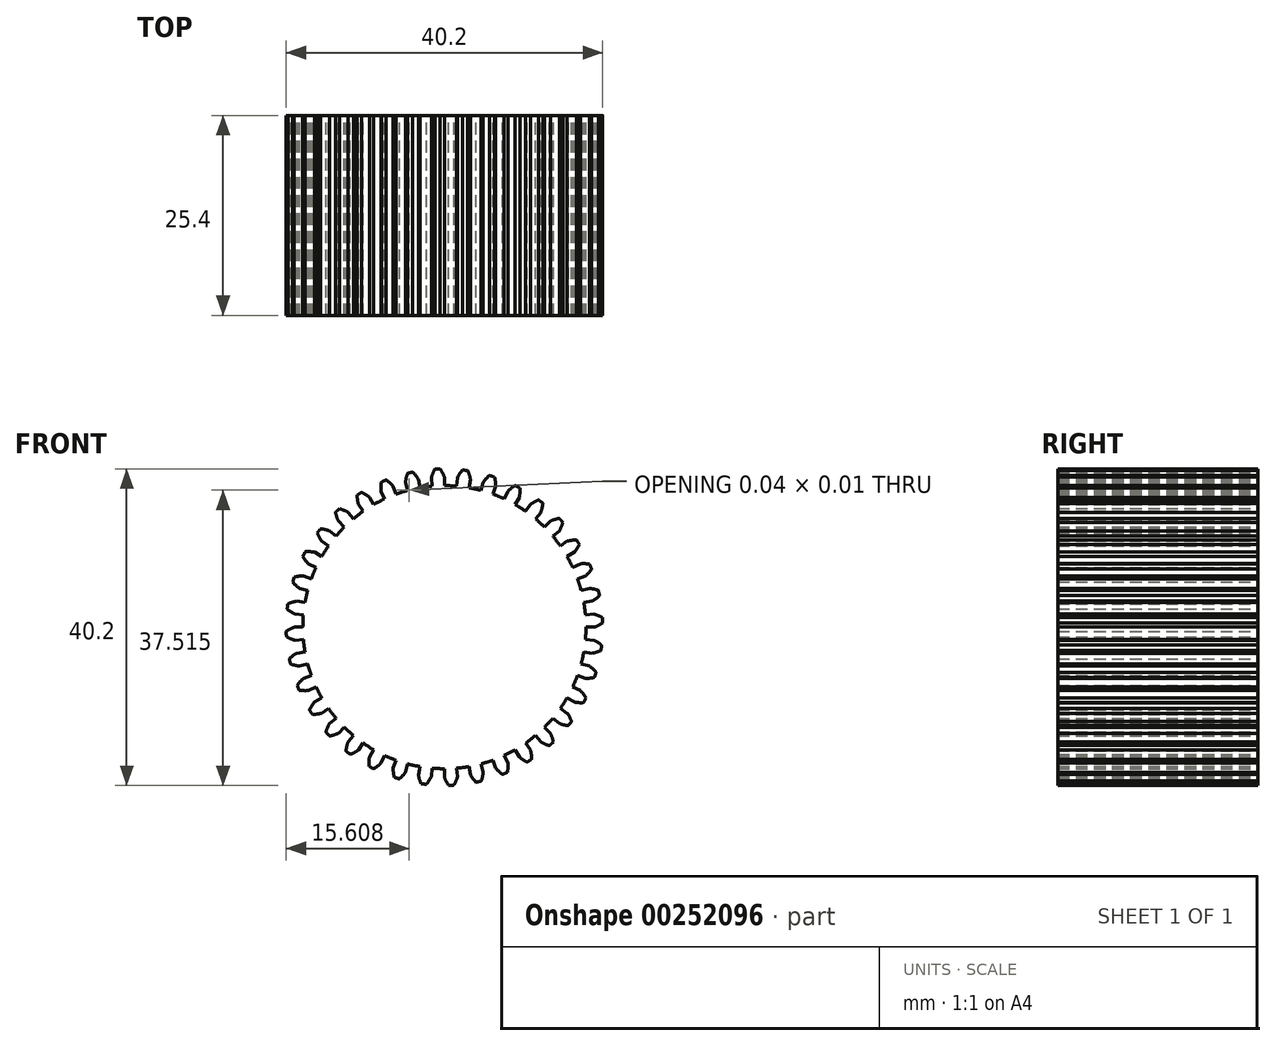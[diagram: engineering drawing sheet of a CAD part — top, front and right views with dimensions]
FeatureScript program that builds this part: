
annotation { "Feature Type Name" : "Feature", "Feature Type Description" : "" }
export const myFeature = defineFeature(function(context is Context, id is Id, definition is map)
    precondition{}
    {
        {
            var Q0;
            Q0=qCreatedBy(makeId("Front.planeOp"),FACE);
            var sketch = newSketch(context, id + "F0", { "sketchPlane" : qUnion([Q0])});
            skArc(sketch, "E0", {"start": v(-0.54, 20.1) * mm, "mid": v(-0.7, 20.1) * mm, "end": v(-0.88, 20.08) * mm});
            skArc(sketch, "E1", {"start": v(1.57, 17.91) * mm, "mid": v(0.7, 17.97) * mm, "end": v(-0.19, 17.98) * mm});
            skLineSegment(sketch, "E2", {"start": v(0, 17.98) * mm, "end": v(0, 19.05) * mm});
            skLineSegment(sketch, "E3", {"start": v(-4.48, 17.42) * mm, "end": v(-4.51, 17.4) * mm});
            skLineSegment(sketch, "E4", {"start": v(0, 0) * mm, "end": v(-0.88, 20.08) * mm});
            skArc(sketch, "E5", {"start": v(4.45, 17.34) * mm, "mid": v(4.46, 17.38) * mm, "end": v(4.47, 17.42) * mm});
            skArc(sketch, "E6.trimOffspring", {"start": v(0, 19.05) * mm, "mid": v(-0.24, 19.6) * mm, "end": v(-0.54, 20.1) * mm});
            skArc(sketch, "E7.trimOffspring", {"start": v(-4.48, 17.42) * mm, "mid": v(-4.46, 17.38) * mm, "end": v(-4.45, 17.34) * mm});
            skLineSegment(sketch, "E8.trimOffspring", {"start": v(-1.66, 18.98) * mm, "end": v(-1.67, 19.05) * mm});
            skArc(sketch, "E9.trimOffspring", {"start": v(-8.95, 15.8) * mm, "mid": v(-8.9, 15.67) * mm, "end": v(-8.86, 15.56) * mm});
            skLineSegment(sketch, "E10.MirrorCS", {"start": v(-1.57, 17.91) * mm, "end": v(-1.66, 18.98) * mm});
            skArc(sketch, "E11.MirrorCS", {"start": v(-1.66, 18.98) * mm, "mid": v(-1.47, 19.54) * mm, "end": v(-1.22, 20.07) * mm});
            skArc(sketch, "E12.MirrorCS", {"start": v(-1.22, 20.07) * mm, "mid": v(-1.05, 20.08) * mm, "end": v(-0.88, 20.08) * mm});
            skLineSegment(sketch, "E13.1.0", {"start": v(-4.65, 17.37) * mm, "end": v(-4.93, 18.4) * mm});
            skArc(sketch, "E13.1.1", {"start": v(-4.93, 18.4) * mm, "mid": v(-4.84, 18.98) * mm, "end": v(-4.68, 19.55) * mm});
            skArc(sketch, "E13.1.2", {"start": v(-4.68, 19.55) * mm, "mid": v(-4.52, 19.59) * mm, "end": v(-4.35, 19.63) * mm});
            skArc(sketch, "E13.1.3", {"start": v(-4.02, 19.7) * mm, "mid": v(-4.18, 19.66) * mm, "end": v(-4.35, 19.63) * mm});
            skArc(sketch, "E13.1.4", {"start": v(-3.3, 18.76) * mm, "mid": v(-3.63, 19.25) * mm, "end": v(-4.02, 19.7) * mm});
            skLineSegment(sketch, "E13.1.5", {"start": v(-3.12, 17.7) * mm, "end": v(-3.3, 18.76) * mm});
            skLineSegment(sketch, "E13.2.0", {"start": v(-7.6, 16.3) * mm, "end": v(-8.05, 17.27) * mm});
            skArc(sketch, "E13.2.1", {"start": v(-8.05, 17.27) * mm, "mid": v(-8.07, 17.85) * mm, "end": v(-8, 18.44) * mm});
            skArc(sketch, "E13.2.2", {"start": v(-8, 18.44) * mm, "mid": v(-7.85, 18.5) * mm, "end": v(-7.7, 18.57) * mm});
            skArc(sketch, "E13.2.3", {"start": v(-7.38, 18.7) * mm, "mid": v(-7.54, 18.64) * mm, "end": v(-7.7, 18.57) * mm});
            skArc(sketch, "E13.2.4", {"start": v(-6.52, 17.9) * mm, "mid": v(-6.92, 18.33) * mm, "end": v(-7.38, 18.7) * mm});
            skLineSegment(sketch, "E13.2.5", {"start": v(-6.15, 16.9) * mm, "end": v(-6.52, 17.9) * mm});
            skLineSegment(sketch, "E13.3.0", {"start": v(-10.31, 14.73) * mm, "end": v(-10.93, 15.6) * mm});
            skArc(sketch, "E13.3.1", {"start": v(-10.93, 15.6) * mm, "mid": v(-11.04, 16.18) * mm, "end": v(-11.09, 16.77) * mm});
            skArc(sketch, "E13.3.2", {"start": v(-11.09, 16.77) * mm, "mid": v(-10.95, 16.86) * mm, "end": v(-10.8, 16.96) * mm});
            skArc(sketch, "E13.3.3", {"start": v(-10.51, 17.14) * mm, "mid": v(-10.66, 17.05) * mm, "end": v(-10.8, 16.96) * mm});
            skArc(sketch, "E13.3.4", {"start": v(-9.52, 16.5) * mm, "mid": v(-10, 16.85) * mm, "end": v(-10.51, 17.14) * mm});
            skLineSegment(sketch, "E13.3.5", {"start": v(-9, 15.57) * mm, "end": v(-9.53, 16.5) * mm});
            skLineSegment(sketch, "E13.4.0", {"start": v(-12.72, 12.72) * mm, "end": v(-13.47, 13.47) * mm});
            skArc(sketch, "E13.4.1", {"start": v(-13.47, 13.47) * mm, "mid": v(-13.69, 14.02) * mm, "end": v(-13.83, 14.6) * mm});
            skArc(sketch, "E13.4.2", {"start": v(-13.83, 14.6) * mm, "mid": v(-13.7, 14.7) * mm, "end": v(-13.58, 14.82) * mm});
            skArc(sketch, "E13.4.3", {"start": v(-13.33, 15.05) * mm, "mid": v(-13.46, 14.94) * mm, "end": v(-13.58, 14.82) * mm});
            skArc(sketch, "E13.4.4", {"start": v(-12.25, 14.6) * mm, "mid": v(-12.77, 14.86) * mm, "end": v(-13.33, 15.05) * mm});
            skLineSegment(sketch, "E13.4.5", {"start": v(-11.56, 13.78) * mm, "end": v(-12.25, 14.6) * mm});
            skLineSegment(sketch, "E13.5.0", {"start": v(-14.73, 10.31) * mm, "end": v(-15.6, 10.93) * mm});
            skArc(sketch, "E13.5.1", {"start": v(-15.6, 10.93) * mm, "mid": v(-15.91, 11.43) * mm, "end": v(-16.15, 11.97) * mm});
            skArc(sketch, "E13.5.2", {"start": v(-16.15, 11.97) * mm, "mid": v(-16.05, 12.1) * mm, "end": v(-15.95, 12.24) * mm});
            skArc(sketch, "E13.5.3", {"start": v(-15.74, 12.5) * mm, "mid": v(-15.85, 12.37) * mm, "end": v(-15.95, 12.24) * mm});
            skArc(sketch, "E13.5.4", {"start": v(-14.6, 12.25) * mm, "mid": v(-15.16, 12.41) * mm, "end": v(-15.74, 12.5) * mm});
            skLineSegment(sketch, "E13.5.5", {"start": v(-13.78, 11.56) * mm, "end": v(-14.6, 12.25) * mm});
            skLineSegment(sketch, "E13.6.0", {"start": v(-16.3, 7.6) * mm, "end": v(-17.27, 8.05) * mm});
            skArc(sketch, "E13.6.1", {"start": v(-17.27, 8.05) * mm, "mid": v(-17.65, 8.5) * mm, "end": v(-17.99, 8.98) * mm});
            skArc(sketch, "E13.6.2", {"start": v(-17.99, 8.98) * mm, "mid": v(-17.91, 9.13) * mm, "end": v(-17.83, 9.28) * mm});
            skArc(sketch, "E13.6.3", {"start": v(-17.67, 9.58) * mm, "mid": v(-17.75, 9.43) * mm, "end": v(-17.83, 9.28) * mm});
            skArc(sketch, "E13.6.4", {"start": v(-16.5, 9.53) * mm, "mid": v(-17.08, 9.6) * mm, "end": v(-17.67, 9.58) * mm});
            skLineSegment(sketch, "E13.6.5", {"start": v(-15.57, 9) * mm, "end": v(-16.5, 9.53) * mm});
            skLineSegment(sketch, "E13.7.0", {"start": v(-17.37, 4.65) * mm, "end": v(-18.4, 4.93) * mm});
            skArc(sketch, "E13.7.1", {"start": v(-18.4, 4.93) * mm, "mid": v(-18.86, 5.3) * mm, "end": v(-19.27, 5.72) * mm});
            skArc(sketch, "E13.7.2", {"start": v(-19.27, 5.72) * mm, "mid": v(-19.22, 5.88) * mm, "end": v(-19.17, 6.05) * mm});
            skArc(sketch, "E13.7.3", {"start": v(-19.07, 6.37) * mm, "mid": v(-19.12, 6.2) * mm, "end": v(-19.17, 6.05) * mm});
            skArc(sketch, "E13.7.4", {"start": v(-17.9, 6.52) * mm, "mid": v(-18.49, 6.48) * mm, "end": v(-19.07, 6.37) * mm});
            skLineSegment(sketch, "E13.7.5", {"start": v(-16.9, 6.15) * mm, "end": v(-17.9, 6.52) * mm});
            skLineSegment(sketch, "E13.8.0", {"start": v(-17.91, 1.57) * mm, "end": v(-18.98, 1.66) * mm});
            skArc(sketch, "E13.8.1", {"start": v(-18.98, 1.66) * mm, "mid": v(-19.5, 1.94) * mm, "end": v(-19.97, 2.29) * mm});
            skArc(sketch, "E13.8.2", {"start": v(-19.97, 2.29) * mm, "mid": v(-19.95, 2.46) * mm, "end": v(-19.93, 2.62) * mm});
            skArc(sketch, "E13.8.3", {"start": v(-19.88, 2.96) * mm, "mid": v(-19.9, 2.8) * mm, "end": v(-19.93, 2.62) * mm});
            skArc(sketch, "E13.8.4", {"start": v(-18.76, 3.3) * mm, "mid": v(-19.33, 3.17) * mm, "end": v(-19.88, 2.96) * mm});
            skLineSegment(sketch, "E13.8.5", {"start": v(-17.7, 3.12) * mm, "end": v(-18.76, 3.3) * mm});
            skLineSegment(sketch, "E13.9.0", {"start": v(-17.91, -1.57) * mm, "end": v(-18.98, -1.66) * mm});
            skArc(sketch, "E13.9.1", {"start": v(-18.98, -1.66) * mm, "mid": v(-19.54, -1.47) * mm, "end": v(-20.07, -1.22) * mm});
            skArc(sketch, "E13.9.2", {"start": v(-20.07, -1.22) * mm, "mid": v(-20.08, -1.05) * mm, "end": v(-20.08, -0.88) * mm});
            skArc(sketch, "E13.9.3", {"start": v(-20.1, -0.54) * mm, "mid": v(-20.1, -0.7) * mm, "end": v(-20.08, -0.88) * mm});
            skArc(sketch, "E13.9.4", {"start": v(-19.05, 0) * mm, "mid": v(-19.6, -0.24) * mm, "end": v(-20.1, -0.54) * mm});
            skLineSegment(sketch, "E13.9.5", {"start": v(-17.98, 0) * mm, "end": v(-19.05, 0) * mm});
            skLineSegment(sketch, "E13.10.0", {"start": v(-17.37, -4.65) * mm, "end": v(-18.4, -4.93) * mm});
            skArc(sketch, "E13.10.1", {"start": v(-18.4, -4.93) * mm, "mid": v(-18.98, -4.84) * mm, "end": v(-19.55, -4.68) * mm});
            skArc(sketch, "E13.10.2", {"start": v(-19.55, -4.68) * mm, "mid": v(-19.59, -4.52) * mm, "end": v(-19.63, -4.35) * mm});
            skArc(sketch, "E13.10.3", {"start": v(-19.7, -4.02) * mm, "mid": v(-19.66, -4.18) * mm, "end": v(-19.63, -4.35) * mm});
            skArc(sketch, "E13.10.4", {"start": v(-18.76, -3.3) * mm, "mid": v(-19.25, -3.63) * mm, "end": v(-19.7, -4.02) * mm});
            skLineSegment(sketch, "E13.10.5", {"start": v(-17.7, -3.12) * mm, "end": v(-18.76, -3.3) * mm});
            skLineSegment(sketch, "E13.11.0", {"start": v(-16.3, -7.6) * mm, "end": v(-17.27, -8.05) * mm});
            skArc(sketch, "E13.11.1", {"start": v(-17.27, -8.05) * mm, "mid": v(-17.85, -8.07) * mm, "end": v(-18.44, -8) * mm});
            skArc(sketch, "E13.11.2", {"start": v(-18.44, -8) * mm, "mid": v(-18.5, -7.85) * mm, "end": v(-18.57, -7.7) * mm});
            skArc(sketch, "E13.11.3", {"start": v(-18.7, -7.38) * mm, "mid": v(-18.64, -7.54) * mm, "end": v(-18.57, -7.7) * mm});
            skArc(sketch, "E13.11.4", {"start": v(-17.9, -6.52) * mm, "mid": v(-18.33, -6.92) * mm, "end": v(-18.7, -7.38) * mm});
            skLineSegment(sketch, "E13.11.5", {"start": v(-16.9, -6.15) * mm, "end": v(-17.9, -6.52) * mm});
            skLineSegment(sketch, "E13.12.0", {"start": v(-14.73, -10.31) * mm, "end": v(-15.6, -10.93) * mm});
            skArc(sketch, "E13.12.1", {"start": v(-15.6, -10.93) * mm, "mid": v(-16.18, -11.04) * mm, "end": v(-16.77, -11.09) * mm});
            skArc(sketch, "E13.12.2", {"start": v(-16.77, -11.09) * mm, "mid": v(-16.86, -10.95) * mm, "end": v(-16.96, -10.8) * mm});
            skArc(sketch, "E13.12.3", {"start": v(-17.14, -10.51) * mm, "mid": v(-17.05, -10.66) * mm, "end": v(-16.96, -10.8) * mm});
            skArc(sketch, "E13.12.4", {"start": v(-16.5, -9.52) * mm, "mid": v(-16.85, -10) * mm, "end": v(-17.14, -10.51) * mm});
            skLineSegment(sketch, "E13.12.5", {"start": v(-15.57, -9) * mm, "end": v(-16.5, -9.52) * mm});
            skLineSegment(sketch, "E13.13.0", {"start": v(-12.72, -12.72) * mm, "end": v(-13.47, -13.47) * mm});
            skArc(sketch, "E13.13.1", {"start": v(-13.47, -13.47) * mm, "mid": v(-14.02, -13.69) * mm, "end": v(-14.6, -13.83) * mm});
            skArc(sketch, "E13.13.2", {"start": v(-14.6, -13.83) * mm, "mid": v(-14.7, -13.7) * mm, "end": v(-14.82, -13.58) * mm});
            skArc(sketch, "E13.13.3", {"start": v(-15.05, -13.33) * mm, "mid": v(-14.94, -13.46) * mm, "end": v(-14.82, -13.58) * mm});
            skArc(sketch, "E13.13.4", {"start": v(-14.6, -12.25) * mm, "mid": v(-14.86, -12.77) * mm, "end": v(-15.05, -13.33) * mm});
            skLineSegment(sketch, "E13.13.5", {"start": v(-13.78, -11.56) * mm, "end": v(-14.6, -12.25) * mm});
            skLineSegment(sketch, "E13.14.0", {"start": v(-10.31, -14.73) * mm, "end": v(-10.93, -15.6) * mm});
            skArc(sketch, "E13.14.1", {"start": v(-10.93, -15.6) * mm, "mid": v(-11.43, -15.91) * mm, "end": v(-11.97, -16.15) * mm});
            skArc(sketch, "E13.14.2", {"start": v(-11.97, -16.15) * mm, "mid": v(-12.1, -16.05) * mm, "end": v(-12.24, -15.95) * mm});
            skArc(sketch, "E13.14.3", {"start": v(-12.5, -15.74) * mm, "mid": v(-12.37, -15.85) * mm, "end": v(-12.24, -15.95) * mm});
            skArc(sketch, "E13.14.4", {"start": v(-12.25, -14.6) * mm, "mid": v(-12.41, -15.16) * mm, "end": v(-12.5, -15.74) * mm});
            skLineSegment(sketch, "E13.14.5", {"start": v(-11.56, -13.78) * mm, "end": v(-12.25, -14.6) * mm});
            skLineSegment(sketch, "E13.15.0", {"start": v(-7.6, -16.3) * mm, "end": v(-8.05, -17.27) * mm});
            skArc(sketch, "E13.15.1", {"start": v(-8.05, -17.27) * mm, "mid": v(-8.5, -17.65) * mm, "end": v(-8.98, -17.99) * mm});
            skArc(sketch, "E13.15.2", {"start": v(-8.98, -17.99) * mm, "mid": v(-9.13, -17.91) * mm, "end": v(-9.28, -17.83) * mm});
            skArc(sketch, "E13.15.3", {"start": v(-9.58, -17.67) * mm, "mid": v(-9.43, -17.75) * mm, "end": v(-9.28, -17.83) * mm});
            skArc(sketch, "E13.15.4", {"start": v(-9.53, -16.5) * mm, "mid": v(-9.6, -17.08) * mm, "end": v(-9.58, -17.67) * mm});
            skLineSegment(sketch, "E13.15.5", {"start": v(-9, -15.57) * mm, "end": v(-9.53, -16.5) * mm});
            skLineSegment(sketch, "E13.16.0", {"start": v(-4.65, -17.37) * mm, "end": v(-4.93, -18.4) * mm});
            skArc(sketch, "E13.16.1", {"start": v(-4.93, -18.4) * mm, "mid": v(-5.3, -18.86) * mm, "end": v(-5.72, -19.27) * mm});
            skArc(sketch, "E13.16.2", {"start": v(-5.72, -19.27) * mm, "mid": v(-5.88, -19.22) * mm, "end": v(-6.05, -19.17) * mm});
            skArc(sketch, "E13.16.3", {"start": v(-6.37, -19.07) * mm, "mid": v(-6.2, -19.12) * mm, "end": v(-6.05, -19.17) * mm});
            skArc(sketch, "E13.16.4", {"start": v(-6.52, -17.9) * mm, "mid": v(-6.48, -18.49) * mm, "end": v(-6.37, -19.07) * mm});
            skLineSegment(sketch, "E13.16.5", {"start": v(-6.15, -16.9) * mm, "end": v(-6.52, -17.9) * mm});
            skLineSegment(sketch, "E13.17.0", {"start": v(-1.57, -17.91) * mm, "end": v(-1.66, -18.98) * mm});
            skArc(sketch, "E13.17.1", {"start": v(-1.66, -18.98) * mm, "mid": v(-1.94, -19.5) * mm, "end": v(-2.29, -19.97) * mm});
            skArc(sketch, "E13.17.2", {"start": v(-2.29, -19.97) * mm, "mid": v(-2.46, -19.95) * mm, "end": v(-2.62, -19.93) * mm});
            skArc(sketch, "E13.17.3", {"start": v(-2.96, -19.88) * mm, "mid": v(-2.8, -19.9) * mm, "end": v(-2.62, -19.93) * mm});
            skArc(sketch, "E13.17.4", {"start": v(-3.3, -18.76) * mm, "mid": v(-3.17, -19.33) * mm, "end": v(-2.96, -19.88) * mm});
            skLineSegment(sketch, "E13.17.5", {"start": v(-3.12, -17.7) * mm, "end": v(-3.3, -18.76) * mm});
            skLineSegment(sketch, "E13.18.0", {"start": v(1.57, -17.91) * mm, "end": v(1.66, -18.98) * mm});
            skArc(sketch, "E13.18.1", {"start": v(1.66, -18.98) * mm, "mid": v(1.47, -19.54) * mm, "end": v(1.22, -20.07) * mm});
            skArc(sketch, "E13.18.2", {"start": v(1.22, -20.07) * mm, "mid": v(1.05, -20.08) * mm, "end": v(0.88, -20.08) * mm});
            skArc(sketch, "E13.18.3", {"start": v(0.54, -20.1) * mm, "mid": v(0.7, -20.1) * mm, "end": v(0.88, -20.08) * mm});
            skArc(sketch, "E13.18.4", {"start": v(0, -19.05) * mm, "mid": v(0.24, -19.6) * mm, "end": v(0.54, -20.1) * mm});
            skLineSegment(sketch, "E13.18.5", {"start": v(0, -17.98) * mm, "end": v(0, -19.05) * mm});
            skLineSegment(sketch, "E13.19.0", {"start": v(4.65, -17.37) * mm, "end": v(4.93, -18.4) * mm});
            skArc(sketch, "E13.19.1", {"start": v(4.93, -18.4) * mm, "mid": v(4.84, -18.98) * mm, "end": v(4.68, -19.55) * mm});
            skArc(sketch, "E13.19.2", {"start": v(4.68, -19.55) * mm, "mid": v(4.52, -19.59) * mm, "end": v(4.35, -19.63) * mm});
            skArc(sketch, "E13.19.3", {"start": v(4.02, -19.7) * mm, "mid": v(4.18, -19.66) * mm, "end": v(4.35, -19.63) * mm});
            skArc(sketch, "E13.19.4", {"start": v(3.3, -18.76) * mm, "mid": v(3.63, -19.25) * mm, "end": v(4.02, -19.7) * mm});
            skLineSegment(sketch, "E13.19.5", {"start": v(3.12, -17.7) * mm, "end": v(3.3, -18.76) * mm});
            skLineSegment(sketch, "E13.20.0", {"start": v(7.6, -16.3) * mm, "end": v(8.05, -17.27) * mm});
            skArc(sketch, "E13.20.1", {"start": v(8.05, -17.27) * mm, "mid": v(8.07, -17.85) * mm, "end": v(8, -18.44) * mm});
            skArc(sketch, "E13.20.2", {"start": v(8, -18.44) * mm, "mid": v(7.85, -18.5) * mm, "end": v(7.7, -18.57) * mm});
            skArc(sketch, "E13.20.3", {"start": v(7.38, -18.7) * mm, "mid": v(7.54, -18.64) * mm, "end": v(7.7, -18.57) * mm});
            skArc(sketch, "E13.20.4", {"start": v(6.52, -17.9) * mm, "mid": v(6.92, -18.33) * mm, "end": v(7.38, -18.7) * mm});
            skLineSegment(sketch, "E13.20.5", {"start": v(6.15, -16.9) * mm, "end": v(6.52, -17.9) * mm});
            skLineSegment(sketch, "E13.21.0", {"start": v(10.31, -14.73) * mm, "end": v(10.93, -15.6) * mm});
            skArc(sketch, "E13.21.1", {"start": v(10.93, -15.6) * mm, "mid": v(11.04, -16.18) * mm, "end": v(11.09, -16.77) * mm});
            skArc(sketch, "E13.21.2", {"start": v(11.09, -16.77) * mm, "mid": v(10.95, -16.86) * mm, "end": v(10.8, -16.96) * mm});
            skArc(sketch, "E13.21.3", {"start": v(10.51, -17.14) * mm, "mid": v(10.66, -17.05) * mm, "end": v(10.8, -16.96) * mm});
            skArc(sketch, "E13.21.4", {"start": v(9.52, -16.5) * mm, "mid": v(10, -16.85) * mm, "end": v(10.51, -17.14) * mm});
            skLineSegment(sketch, "E13.21.5", {"start": v(9, -15.57) * mm, "end": v(9.53, -16.5) * mm});
            skLineSegment(sketch, "E13.22.0", {"start": v(12.72, -12.72) * mm, "end": v(13.47, -13.47) * mm});
            skArc(sketch, "E13.22.1", {"start": v(13.47, -13.47) * mm, "mid": v(13.69, -14.02) * mm, "end": v(13.83, -14.6) * mm});
            skArc(sketch, "E13.22.2", {"start": v(13.83, -14.6) * mm, "mid": v(13.7, -14.7) * mm, "end": v(13.58, -14.82) * mm});
            skArc(sketch, "E13.22.3", {"start": v(13.33, -15.05) * mm, "mid": v(13.46, -14.94) * mm, "end": v(13.58, -14.82) * mm});
            skArc(sketch, "E13.22.4", {"start": v(12.25, -14.6) * mm, "mid": v(12.77, -14.86) * mm, "end": v(13.33, -15.05) * mm});
            skLineSegment(sketch, "E13.22.5", {"start": v(11.56, -13.78) * mm, "end": v(12.25, -14.6) * mm});
            skLineSegment(sketch, "E13.23.0", {"start": v(14.73, -10.31) * mm, "end": v(15.6, -10.93) * mm});
            skArc(sketch, "E13.23.1", {"start": v(15.6, -10.93) * mm, "mid": v(15.91, -11.43) * mm, "end": v(16.15, -11.97) * mm});
            skArc(sketch, "E13.23.2", {"start": v(16.15, -11.97) * mm, "mid": v(16.05, -12.1) * mm, "end": v(15.95, -12.24) * mm});
            skArc(sketch, "E13.23.3", {"start": v(15.74, -12.5) * mm, "mid": v(15.85, -12.37) * mm, "end": v(15.95, -12.24) * mm});
            skArc(sketch, "E13.23.4", {"start": v(14.6, -12.25) * mm, "mid": v(15.16, -12.41) * mm, "end": v(15.74, -12.5) * mm});
            skLineSegment(sketch, "E13.23.5", {"start": v(13.78, -11.56) * mm, "end": v(14.6, -12.25) * mm});
            skLineSegment(sketch, "E13.24.0", {"start": v(16.3, -7.6) * mm, "end": v(17.27, -8.05) * mm});
            skArc(sketch, "E13.24.1", {"start": v(17.27, -8.05) * mm, "mid": v(17.65, -8.5) * mm, "end": v(17.99, -8.98) * mm});
            skArc(sketch, "E13.24.2", {"start": v(17.99, -8.98) * mm, "mid": v(17.91, -9.13) * mm, "end": v(17.83, -9.28) * mm});
            skArc(sketch, "E13.24.3", {"start": v(17.67, -9.58) * mm, "mid": v(17.75, -9.43) * mm, "end": v(17.83, -9.28) * mm});
            skArc(sketch, "E13.24.4", {"start": v(16.5, -9.53) * mm, "mid": v(17.08, -9.6) * mm, "end": v(17.67, -9.58) * mm});
            skLineSegment(sketch, "E13.24.5", {"start": v(15.57, -9) * mm, "end": v(16.5, -9.53) * mm});
            skLineSegment(sketch, "E13.25.0", {"start": v(17.37, -4.65) * mm, "end": v(18.4, -4.93) * mm});
            skArc(sketch, "E13.25.1", {"start": v(18.4, -4.93) * mm, "mid": v(18.86, -5.3) * mm, "end": v(19.27, -5.72) * mm});
            skArc(sketch, "E13.25.2", {"start": v(19.27, -5.72) * mm, "mid": v(19.22, -5.88) * mm, "end": v(19.17, -6.05) * mm});
            skArc(sketch, "E13.25.3", {"start": v(19.07, -6.37) * mm, "mid": v(19.12, -6.2) * mm, "end": v(19.17, -6.05) * mm});
            skArc(sketch, "E13.25.4", {"start": v(17.9, -6.52) * mm, "mid": v(18.49, -6.48) * mm, "end": v(19.07, -6.37) * mm});
            skLineSegment(sketch, "E13.25.5", {"start": v(16.9, -6.15) * mm, "end": v(17.9, -6.52) * mm});
            skLineSegment(sketch, "E13.26.0", {"start": v(17.91, -1.57) * mm, "end": v(18.98, -1.66) * mm});
            skArc(sketch, "E13.26.1", {"start": v(18.98, -1.66) * mm, "mid": v(19.5, -1.94) * mm, "end": v(19.97, -2.29) * mm});
            skArc(sketch, "E13.26.2", {"start": v(19.97, -2.29) * mm, "mid": v(19.95, -2.46) * mm, "end": v(19.93, -2.62) * mm});
            skArc(sketch, "E13.26.3", {"start": v(19.88, -2.96) * mm, "mid": v(19.9, -2.8) * mm, "end": v(19.93, -2.62) * mm});
            skArc(sketch, "E13.26.4", {"start": v(18.76, -3.3) * mm, "mid": v(19.33, -3.17) * mm, "end": v(19.88, -2.96) * mm});
            skLineSegment(sketch, "E13.26.5", {"start": v(17.7, -3.12) * mm, "end": v(18.76, -3.3) * mm});
            skLineSegment(sketch, "E13.27.0", {"start": v(17.91, 1.57) * mm, "end": v(18.98, 1.66) * mm});
            skArc(sketch, "E13.27.1", {"start": v(18.98, 1.66) * mm, "mid": v(19.54, 1.47) * mm, "end": v(20.07, 1.22) * mm});
            skArc(sketch, "E13.27.2", {"start": v(20.07, 1.22) * mm, "mid": v(20.08, 1.05) * mm, "end": v(20.08, 0.88) * mm});
            skArc(sketch, "E13.27.3", {"start": v(20.1, 0.54) * mm, "mid": v(20.1, 0.7) * mm, "end": v(20.08, 0.88) * mm});
            skArc(sketch, "E13.27.4", {"start": v(19.05, 0) * mm, "mid": v(19.6, 0.24) * mm, "end": v(20.1, 0.54) * mm});
            skLineSegment(sketch, "E13.27.5", {"start": v(17.98, 0) * mm, "end": v(19.05, 0) * mm});
            skLineSegment(sketch, "E13.28.0", {"start": v(17.37, 4.65) * mm, "end": v(18.4, 4.93) * mm});
            skArc(sketch, "E13.28.1", {"start": v(18.4, 4.93) * mm, "mid": v(18.98, 4.84) * mm, "end": v(19.55, 4.68) * mm});
            skArc(sketch, "E13.28.2", {"start": v(19.55, 4.68) * mm, "mid": v(19.59, 4.52) * mm, "end": v(19.63, 4.35) * mm});
            skArc(sketch, "E13.28.3", {"start": v(19.7, 4.02) * mm, "mid": v(19.66, 4.18) * mm, "end": v(19.63, 4.35) * mm});
            skArc(sketch, "E13.28.4", {"start": v(18.76, 3.3) * mm, "mid": v(19.25, 3.63) * mm, "end": v(19.7, 4.02) * mm});
            skLineSegment(sketch, "E13.28.5", {"start": v(17.7, 3.12) * mm, "end": v(18.76, 3.3) * mm});
            skLineSegment(sketch, "E13.29.0", {"start": v(16.3, 7.6) * mm, "end": v(17.27, 8.05) * mm});
            skArc(sketch, "E13.29.1", {"start": v(17.27, 8.05) * mm, "mid": v(17.85, 8.07) * mm, "end": v(18.44, 8) * mm});
            skArc(sketch, "E13.29.2", {"start": v(18.44, 8) * mm, "mid": v(18.5, 7.85) * mm, "end": v(18.57, 7.7) * mm});
            skArc(sketch, "E13.29.3", {"start": v(18.7, 7.38) * mm, "mid": v(18.64, 7.54) * mm, "end": v(18.57, 7.7) * mm});
            skArc(sketch, "E13.29.4", {"start": v(17.9, 6.52) * mm, "mid": v(18.33, 6.92) * mm, "end": v(18.7, 7.38) * mm});
            skLineSegment(sketch, "E13.29.5", {"start": v(16.9, 6.15) * mm, "end": v(17.9, 6.52) * mm});
            skLineSegment(sketch, "E13.30.0", {"start": v(14.73, 10.31) * mm, "end": v(15.6, 10.93) * mm});
            skArc(sketch, "E13.30.1", {"start": v(15.6, 10.93) * mm, "mid": v(16.18, 11.04) * mm, "end": v(16.77, 11.09) * mm});
            skArc(sketch, "E13.30.2", {"start": v(16.77, 11.09) * mm, "mid": v(16.86, 10.95) * mm, "end": v(16.96, 10.8) * mm});
            skArc(sketch, "E13.30.3", {"start": v(17.14, 10.51) * mm, "mid": v(17.05, 10.66) * mm, "end": v(16.96, 10.8) * mm});
            skArc(sketch, "E13.30.4", {"start": v(16.5, 9.52) * mm, "mid": v(16.85, 10) * mm, "end": v(17.14, 10.51) * mm});
            skLineSegment(sketch, "E13.30.5", {"start": v(15.57, 9) * mm, "end": v(16.5, 9.52) * mm});
            skLineSegment(sketch, "E13.31.0", {"start": v(12.72, 12.72) * mm, "end": v(13.47, 13.47) * mm});
            skArc(sketch, "E13.31.1", {"start": v(13.47, 13.47) * mm, "mid": v(14.02, 13.69) * mm, "end": v(14.6, 13.83) * mm});
            skArc(sketch, "E13.31.2", {"start": v(14.6, 13.83) * mm, "mid": v(14.7, 13.7) * mm, "end": v(14.82, 13.58) * mm});
            skArc(sketch, "E13.31.3", {"start": v(15.05, 13.33) * mm, "mid": v(14.94, 13.46) * mm, "end": v(14.82, 13.58) * mm});
            skArc(sketch, "E13.31.4", {"start": v(14.6, 12.25) * mm, "mid": v(14.86, 12.77) * mm, "end": v(15.05, 13.33) * mm});
            skLineSegment(sketch, "E13.31.5", {"start": v(13.78, 11.56) * mm, "end": v(14.6, 12.25) * mm});
            skLineSegment(sketch, "E13.32.0", {"start": v(10.31, 14.73) * mm, "end": v(10.93, 15.6) * mm});
            skArc(sketch, "E13.32.1", {"start": v(10.93, 15.6) * mm, "mid": v(11.43, 15.91) * mm, "end": v(11.97, 16.15) * mm});
            skArc(sketch, "E13.32.2", {"start": v(11.97, 16.15) * mm, "mid": v(12.1, 16.05) * mm, "end": v(12.24, 15.95) * mm});
            skArc(sketch, "E13.32.3", {"start": v(12.5, 15.74) * mm, "mid": v(12.37, 15.85) * mm, "end": v(12.24, 15.95) * mm});
            skArc(sketch, "E13.32.4", {"start": v(12.25, 14.6) * mm, "mid": v(12.41, 15.16) * mm, "end": v(12.5, 15.74) * mm});
            skLineSegment(sketch, "E13.32.5", {"start": v(11.56, 13.78) * mm, "end": v(12.25, 14.6) * mm});
            skLineSegment(sketch, "E13.33.0", {"start": v(7.6, 16.3) * mm, "end": v(8.05, 17.27) * mm});
            skArc(sketch, "E13.33.1", {"start": v(8.05, 17.27) * mm, "mid": v(8.5, 17.65) * mm, "end": v(8.98, 17.99) * mm});
            skArc(sketch, "E13.33.2", {"start": v(8.98, 17.99) * mm, "mid": v(9.13, 17.91) * mm, "end": v(9.28, 17.83) * mm});
            skArc(sketch, "E13.33.3", {"start": v(9.58, 17.67) * mm, "mid": v(9.43, 17.75) * mm, "end": v(9.28, 17.83) * mm});
            skArc(sketch, "E13.33.4", {"start": v(9.53, 16.5) * mm, "mid": v(9.6, 17.08) * mm, "end": v(9.58, 17.67) * mm});
            skLineSegment(sketch, "E13.33.5", {"start": v(9, 15.57) * mm, "end": v(9.52, 16.5) * mm});
            skLineSegment(sketch, "E13.34.0", {"start": v(4.65, 17.37) * mm, "end": v(4.93, 18.4) * mm});
            skArc(sketch, "E13.34.1", {"start": v(4.93, 18.4) * mm, "mid": v(5.3, 18.86) * mm, "end": v(5.72, 19.27) * mm});
            skArc(sketch, "E13.34.2", {"start": v(5.72, 19.27) * mm, "mid": v(5.88, 19.22) * mm, "end": v(6.05, 19.17) * mm});
            skArc(sketch, "E13.34.3", {"start": v(6.37, 19.07) * mm, "mid": v(6.2, 19.12) * mm, "end": v(6.05, 19.17) * mm});
            skArc(sketch, "E13.34.4", {"start": v(6.52, 17.9) * mm, "mid": v(6.48, 18.49) * mm, "end": v(6.37, 19.07) * mm});
            skLineSegment(sketch, "E13.34.5", {"start": v(6.15, 16.9) * mm, "end": v(6.52, 17.9) * mm});
            skLineSegment(sketch, "E13.35.0", {"start": v(1.57, 17.91) * mm, "end": v(1.66, 18.98) * mm});
            skArc(sketch, "E13.35.1", {"start": v(1.66, 18.98) * mm, "mid": v(1.94, 19.5) * mm, "end": v(2.29, 19.97) * mm});
            skArc(sketch, "E13.35.2", {"start": v(2.29, 19.97) * mm, "mid": v(2.46, 19.95) * mm, "end": v(2.62, 19.93) * mm});
            skArc(sketch, "E13.35.3", {"start": v(2.96, 19.88) * mm, "mid": v(2.8, 19.9) * mm, "end": v(2.62, 19.93) * mm});
            skArc(sketch, "E13.35.4", {"start": v(3.3, 18.76) * mm, "mid": v(3.17, 19.33) * mm, "end": v(2.96, 19.88) * mm});
            skLineSegment(sketch, "E13.35.5", {"start": v(3.12, 17.7) * mm, "end": v(3.3, 18.76) * mm});
            skArc(sketch, "E14.trimOffspring", {"start": v(4.65, 17.37) * mm, "mid": v(3.9, 17.56) * mm, "end": v(3.12, 17.7) * mm});
            skArc(sketch, "E15.trimOffspring", {"start": v(7.6, 16.3) * mm, "mid": v(6.88, 16.61) * mm, "end": v(6.15, 16.9) * mm});
            skArc(sketch, "E16.trimOffspring", {"start": v(10.31, 14.73) * mm, "mid": v(9.66, 15.17) * mm, "end": v(9, 15.57) * mm});
            skArc(sketch, "E17.trimOffspring", {"start": v(12.85, 12.58) * mm, "mid": v(12.15, 13.26) * mm, "end": v(11.42, 13.9) * mm});
            skArc(sketch, "E18.trimOffspring", {"start": v(14.84, 10.16) * mm, "mid": v(14.27, 10.95) * mm, "end": v(13.66, 11.7) * mm});
            skArc(sketch, "E19.trimOffspring", {"start": v(-1.38, 17.93) * mm, "mid": v(-2.35, 17.83) * mm, "end": v(-3.3, 17.68) * mm});
            skArc(sketch, "E20.trimOffspring", {"start": v(-4.47, 17.42) * mm, "mid": v(-5.32, 17.18) * mm, "end": v(-6.15, 16.9) * mm});
            skArc(sketch, "E21.trimOffspring", {"start": v(-7.43, 16.38) * mm, "mid": v(-8.3, 15.95) * mm, "end": v(-9.15, 15.48) * mm});
            skArc(sketch, "E22.trimOffspring", {"start": v(-12.58, 12.85) * mm, "mid": v(-13.26, 12.15) * mm, "end": v(-13.9, 11.42) * mm});
            skArc(sketch, "E23.trimOffspring", {"start": v(-10.16, 14.84) * mm, "mid": v(-10.95, 14.27) * mm, "end": v(-11.7, 13.66) * mm});
            skArc(sketch, "E24.trimOffspring", {"start": v(-14.62, 10.47) * mm, "mid": v(-15.12, 9.74) * mm, "end": v(-15.57, 9) * mm});
            skArc(sketch, "E25.trimOffspring", {"start": v(-16.22, 7.77) * mm, "mid": v(-16.58, 6.97) * mm, "end": v(-16.9, 6.15) * mm});
            skArc(sketch, "E26.trimOffspring", {"start": v(-17.32, 4.83) * mm, "mid": v(-17.56, 3.9) * mm, "end": v(-17.74, 2.94) * mm});
            skArc(sketch, "E27.trimOffspring", {"start": v(-17.93, -1.38) * mm, "mid": v(-17.83, -2.35) * mm, "end": v(-17.68, -3.3) * mm});
            skArc(sketch, "E28.trimOffspring", {"start": v(-17.9, 1.75) * mm, "mid": v(-17.97, 0.78) * mm, "end": v(-17.98, -0.19) * mm});
            skArc(sketch, "E29.trimOffspring", {"start": v(-17.42, -4.47) * mm, "mid": v(-17.15, -5.4) * mm, "end": v(-16.83, -6.33) * mm});
            skArc(sketch, "E30.trimOffspring", {"start": v(-16.38, -7.43) * mm, "mid": v(-15.95, -8.3) * mm, "end": v(-15.48, -9.15) * mm});
            skArc(sketch, "E31.trimOffspring", {"start": v(-14.84, -10.16) * mm, "mid": v(-14.32, -10.87) * mm, "end": v(-13.78, -11.56) * mm});
            skArc(sketch, "E32.trimOffspring", {"start": v(-12.85, -12.58) * mm, "mid": v(-12.15, -13.26) * mm, "end": v(-11.42, -13.9) * mm});
            skArc(sketch, "E33.trimOffspring", {"start": v(-10.47, -14.62) * mm, "mid": v(-9.74, -15.12) * mm, "end": v(-9, -15.57) * mm});
            skArc(sketch, "E34.trimOffspring", {"start": v(-7.77, -16.22) * mm, "mid": v(-6.88, -16.61) * mm, "end": v(-5.98, -16.96) * mm});
            skArc(sketch, "E35.trimOffspring", {"start": v(-1.75, -17.9) * mm, "mid": v(-0.88, -17.96) * mm, "end": v(0, -17.98) * mm});
            skArc(sketch, "E36.trimOffspring", {"start": v(-4.83, -17.32) * mm, "mid": v(-3.9, -17.56) * mm, "end": v(-2.94, -17.74) * mm});
            skArc(sketch, "E37.trimOffspring", {"start": v(1.38, -17.93) * mm, "mid": v(2.25, -17.84) * mm, "end": v(3.12, -17.7) * mm});
            skArc(sketch, "E38.trimOffspring", {"start": v(4.47, -17.42) * mm, "mid": v(5.32, -17.18) * mm, "end": v(6.15, -16.9) * mm});
            skArc(sketch, "E39.trimOffspring", {"start": v(7.43, -16.38) * mm, "mid": v(7.52, -16.34) * mm, "end": v(7.6, -16.3) * mm});
            skArc(sketch, "E40.trimOffspring", {"start": v(10.16, -14.84) * mm, "mid": v(10.95, -14.27) * mm, "end": v(11.7, -13.66) * mm});
            skArc(sketch, "E41.trimOffspring", {"start": v(12.58, -12.85) * mm, "mid": v(13.2, -12.22) * mm, "end": v(13.78, -11.56) * mm});
            skArc(sketch, "E42.trimOffspring", {"start": v(14.62, -10.47) * mm, "mid": v(15.17, -9.66) * mm, "end": v(15.67, -8.83) * mm});
            skArc(sketch, "E43.trimOffspring", {"start": v(17.32, -4.83) * mm, "mid": v(17.54, -3.98) * mm, "end": v(17.7, -3.12) * mm});
            skArc(sketch, "E44.trimOffspring", {"start": v(16.22, -7.77) * mm, "mid": v(16.61, -6.88) * mm, "end": v(16.96, -5.98) * mm});
            skArc(sketch, "E45.trimOffspring", {"start": v(17.9, -1.75) * mm, "mid": v(17.97, -0.78) * mm, "end": v(17.98, 0.19) * mm});
            skArc(sketch, "E46.trimOffspring", {"start": v(17.93, 1.38) * mm, "mid": v(17.84, 2.25) * mm, "end": v(17.7, 3.12) * mm});
            skArc(sketch, "E47.trimOffspring", {"start": v(17.42, 4.47) * mm, "mid": v(17.15, 5.4) * mm, "end": v(16.83, 6.33) * mm});
            skArc(sketch, "E48.trimOffspring", {"start": v(16.38, 7.43) * mm, "mid": v(15.95, 8.3) * mm, "end": v(15.48, 9.15) * mm});
            skLineSegment(sketch, "E49", {"start": v(7.6, -16.3) * mm, "end": v(9, -15.57) * mm});
            skSolve(sketch);
        }
        {
            var Q0;
            Q0 = qSketchRegion(id + "F0", true);
            extrude(context, id + "F1", {"entities" : qUnion([Q0]), "depth" : 25.4 * mm});
        }
    });
